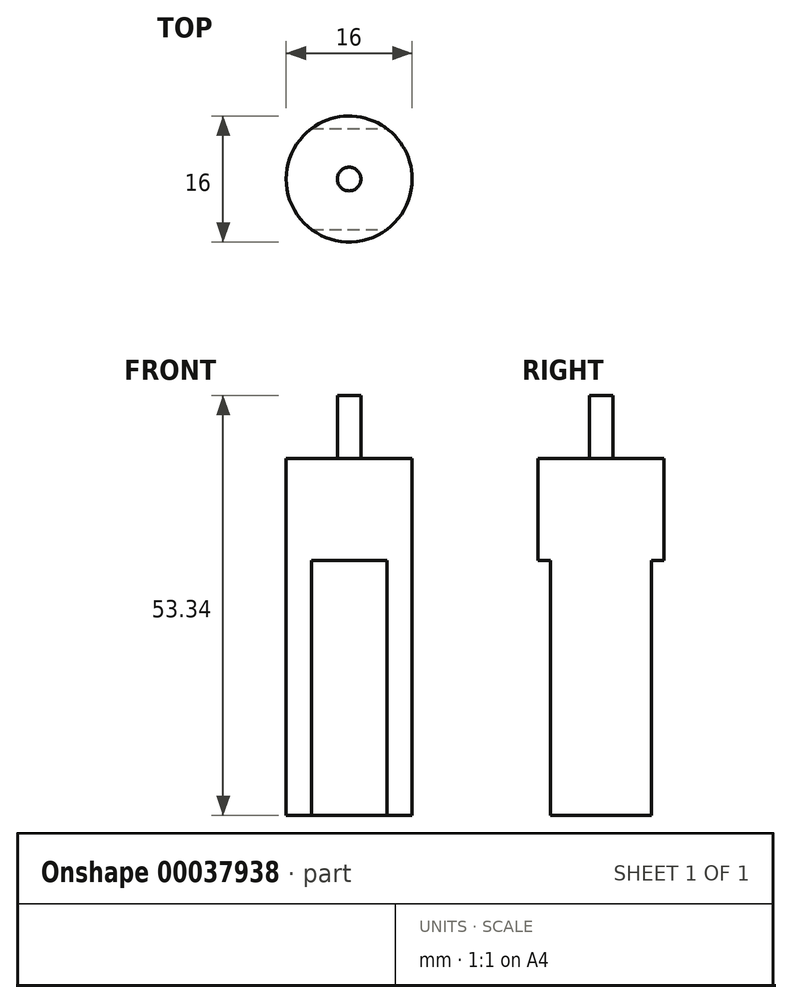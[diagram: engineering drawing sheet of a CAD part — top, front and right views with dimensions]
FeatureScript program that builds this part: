
annotation { "Feature Type Name" : "Feature", "Feature Type Description" : "" }
export const myFeature = defineFeature(function(context is Context, id is Id, definition is map)
    precondition{}
    {
        {
            var Q0;
            Q0=qCreatedBy(makeId("Top.planeOp"),FACE);
            var sketch = newSketch(context, id + "F0", { "sketchPlane" : qUnion([Q0])});
            skCircle(sketch, "E0", {"center": v(0, 0) * mm, "radius": 8 * mm});
            skSolve(sketch);
        }
        {
            var Q0;
            Q0=qSketchRegion(id+"F0",true);
            extrude(context, id + "F1", {"entities" : qUnion([Q0]), "depth" : 45.34 * mm});
        }
        {
            var Q0;
            Q0=makeQuery(id+"F1.opExtrude","CAP_FACE",FACE,{"disambiguationData":[OSD([sQuery(id+"F0.wireOp",EDGE,"E0")])],"isStart":false});
            var sketch = newSketch(context, id + "F2", { "sketchPlane" : qUnion([Q0])});
            skCircle(sketch, "E1", {"center": v(0, 0) * mm, "radius": 1.5 * mm});
            skSolve(sketch);
        }
        {
            var Q0;
            Q0=qSketchRegion(id+"F2",true);
            extrude(context, id + "F3", {"entities" : qUnion([Q0]), "operationType" : NewBodyOperationType.ADD, "depth" : 8 * mm});
        }
        {
            var Q0;
            Q0=makeQuery(id+"F1.opExtrude","CAP_FACE",FACE,{"disambiguationData":[OSD([sQuery(id+"F0.wireOp",EDGE,"E0")])],"isStart":true});
            var sketch = newSketch(context, id + "F4", { "sketchPlane" : qUnion([Q0])});
            skArc(sketch, "E2", {"start": v(4.78, 6.41) * mm, "mid": v(0, 8) * mm, "end": v(-4.78, 6.41) * mm});
            skArc(sketch, "E3", {"start": v(-4.78, -6.41) * mm, "mid": v(0, -8) * mm, "end": v(4.78, -6.41) * mm});
            skLineSegment(sketch, "E4", {"start": v(-4.78, 6.41) * mm, "end": v(4.78, 6.41) * mm});
            skLineSegment(sketch, "E5", {"start": v(-4.78, -6.41) * mm, "end": v(4.78, -6.41) * mm});
            skSolve(sketch);
        }
        {
            var Q0;
            Q0=qSketchRegion(id+"F4",true);
            extrude(context, id + "F5", {"entities" : qUnion([Q0]), "operationType" : NewBodyOperationType.REMOVE, "oppositeDirection" : true, "depth" : 32.4 * mm});
        }
    });
